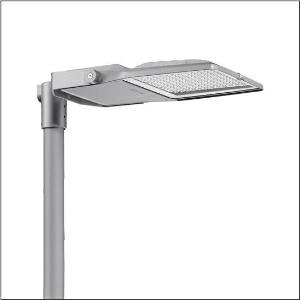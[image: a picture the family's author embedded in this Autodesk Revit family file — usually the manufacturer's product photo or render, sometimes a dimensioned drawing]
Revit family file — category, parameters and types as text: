
# Revit family: floodlight_fl_21_midi___pl64_5xa7786e2e3a_c0a1
name_source: partatom
category: Lighting Fixtures
units: mm (PartAtom-declared; Revit-internal decimal feet)

## family parameters
Cut with Voids When Loaded = No
Host = Face
Light Source = No
Part Type = Normal
Room Calculation Point = No
Round Connector Dimension = Use Diameter
Shared = No

## types (1)
- --- (1 x LED, 26020 lm, 212.4 W, 3000K)
    Apparent Load = 212 VA
    CIE Flux Codes = 28 80 98 100 100
    Color Rendering = 70
    Color Temperature = 3000K
    Default Elevation = 1800 mm
    Description = Floodlight FL 21 midi, floodlight, primary light control with lens, of PMMA, primary optical cover: protective disc, of toughened safety glass, transparent, light distribution: PL64, light emission: direct distribution, installation type: surface-mounted, LED, High Power LED, rated luminous flux: 26.020lm, luminous efficacy: 123lm/W, light colour: 730, colour temperature: 3000K, control gear: ECG Smart Interface, control: flexible luminous flux parameterisation, time-dependent luminous flux control, constant luminous flux control, overheat protection, presetting dimming logarithmic, with terminal, 6-pole, mains connection: 220..240V, AC, 50/60Hz, start of lifetime: 212W, end of service life: 231W, reduction: 95W, luminaire housing, of diecast aluminium, powder-coated, Siteco® metallic grey (DB 702S), corrosivity category C5 mid according to DIN EN ISO 12944, sealing non-destructively replaceable, please order mast flange separately, mast bracket, of steel, galvanised, powder-coated, Siteco® metallic grey (DB 702S), Smart Interface below and above, protection rating (complete): IP66, insulation class (complete): insulation class II (safety insulation), certification: CE, protection symbol: D, impact resistance: IK08, permissible operating ambient temperature: -40..+40°C, permissible operating ambient temperature for outdoor applications: -40..+50°C, standard: DIN EN 12944, LABS conformity tested according to VDMA 24364:2018-05, packaging unit: 1 piece

Light Distribution: PL64
    Height = 76 mm
    Lamp = 1 x LED
    Lamp Light Flux = 26020 lm
    Lamp Power = 212.4 W
    Lamp count = 1
    Length = 657 mm
    Luminous efficacy = 123 lm/W
    Manufacturer = Siteco
    ModVariant = No
    Model = 5XA7786E2E3A
    Number of Poles = 1
    OnlyDefault = Yes
    Power Factor = 1
    Product Name = Floodlight FL 21 midi | PL64
    Product group = floodlight | pylon annexe
    ProductGroupID = 6200
    Protection Class = Protection class II
    Protection Degree = IP 66
    RLX_Detail_Level = 1
    RLX_Emergency_Light_Flux = 0 lm
    RLX_Emergency_Type = 0
    RLX_Emergency_Type_DB = No
    RlxData = <blob elided: 153593 chars, md5=93ce002d>
    Socket = socket
    Standby Power = 0 W
    System Light Flux = 26020 lm
    System Power = 212 W
    Type Comments = factory setting: luminous flux: 100 % | dim-lin: 254 | 710 mA
    Type Image = l_1007123.jpg
    URL = http://relux.com
    VarID = @adj_131755
    Voltage = 0 V
    Weight = 0.00 kg
    Width = 442 mm

## geometry (parser evidence)
native form markers: Blend x4, Sweep x11
no freeform markers — native parametric forms only
